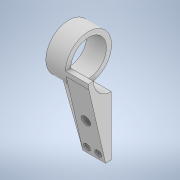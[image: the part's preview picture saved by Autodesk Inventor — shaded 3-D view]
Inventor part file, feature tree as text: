
AUTODESK INVENTOR PART (.ipt)
format: ipt  version: 2021 (Build 250183000, 183)  size: 231,936 bytes
history: native  units: in
note: dims shown in document units (in); Inventor stores cm internally (conversion verified against a paired STEP export)
features: extrude x7, sketch x7, other x7, reference x3, projected_geometry x3, chamfer x1, loft x1, plane x1
ambient origin geometry x8: Origin, YZ Plane, XZ Plane, XY Plane, X Axis, Y Axis, Z Axis, Center Point
bodies: Solid1 (feature_tree)
feature tree (30):
  extrude  "Extrusion1"  Depth=0.3937in
  extrude  "Extrusion2"  Depth=0.3937in TaperAngle=0.0deg
  extrude  "Extrusion3"  Depth=1.5748in TaperAngle=0.0deg
  chamfer  "Chamfer1"  Distance=1.5748in
  extrude  "Extrusion4"  TaperAngle=0.0deg  [1 undecoded]
  extrude  "Extrusion5"  Depth=0.6299in
  loft  "Loft1"
  plane  "Work Plane1"
  extrude  "Extrusion6"  Depth=0.3937in
  extrude  "Extrusion7"  Depth=0.3937in TaperAngle=0.0deg
  sketch  "Sketch1"  dims[d1=0.3937in d2=0.0in d4=0.7874in]
  reference  "Reference1"
  reference  "Reference2"
  sketch  "Sketch2"  dims[d6=0.3937in d7=0.0in d8=0.9843in d9=0.0in]
  reference  "Reference3"
  sketch  "Sketch3"  dims[d10=3.5433in d11=1.378in d12=45.0deg d13=0.9843in d14=0.0in d15=1.5748in d16=0.0in]
  projected_geometry  "Projected Loop1"
  sketch  "Sketch4"  dims[d17=0.0in d18=90.0deg d19=0.0in d20=90.0deg]
  projected_geometry  "Projected Loop2"
  sketch  "Sketch5"  dims[d21=-1.5748in d22=0.6299in]
  projected_geometry  "Projected Loop3"
  other  "Edges1"
  other  "Edges2"
  sketch  "Sketch6"  dims[d23=0.4724in d24=0.4724in]
  sketch  "Sketch7"  dims[d25=1.1811in d26=0.0in d27=2.4803in d28=0.3937in d29=0.0in]
  parser-record x1  (decoder bookkeeping rows leaked as tree rows — omitted from the tree; the rows remain in map.json)
  other  "assembly.iam"
  other  "motor_connector_right:1"
  other  "din_connector_center:2"
  other  "din_connector:1"
note: 1 required parameter value undecoded (feature->parameter linkage not recoverable at this tier; creation-order binding heuristic only, values carry confidence <= 0.55)
note: 1 file-system path scrubbed to <path> (originals preserved in map.json)
